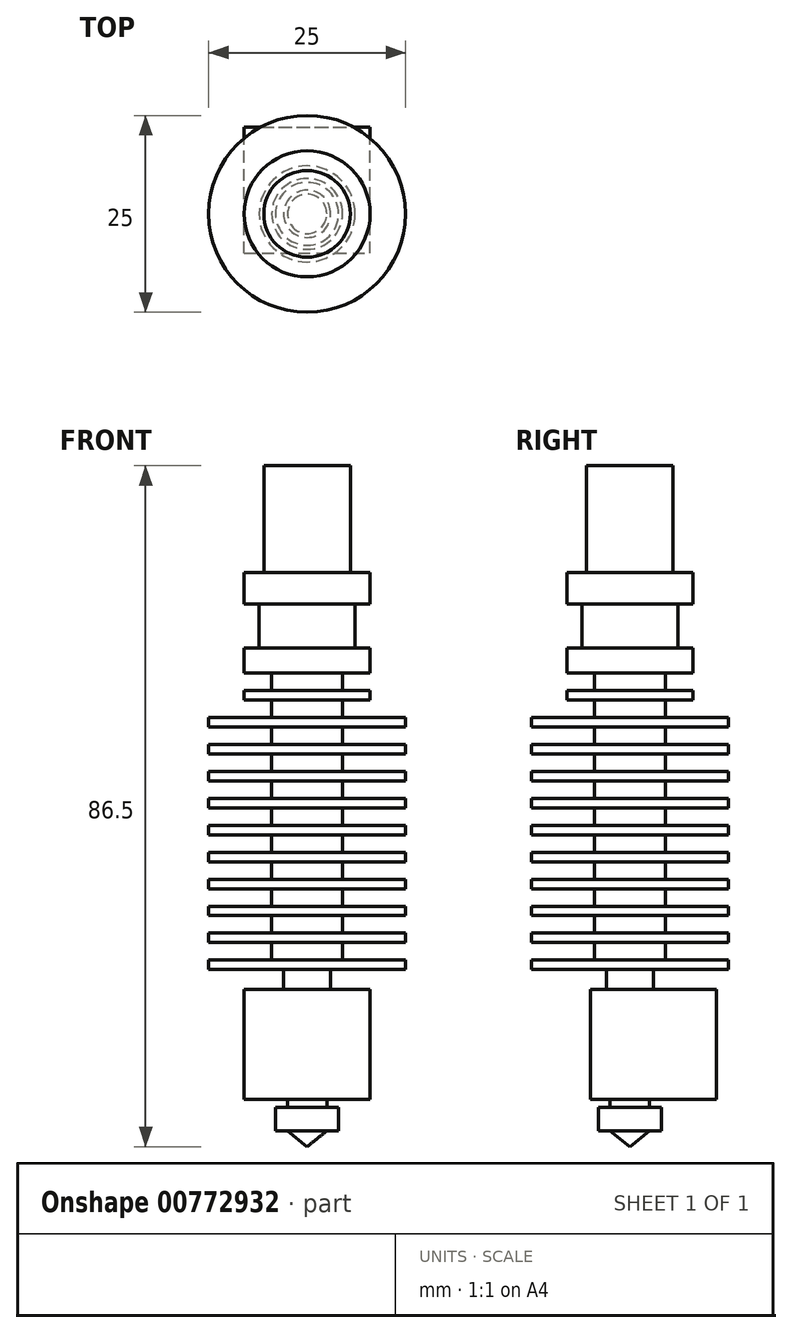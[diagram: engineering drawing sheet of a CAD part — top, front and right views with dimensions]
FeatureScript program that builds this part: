
annotation { "Feature Type Name" : "Feature", "Feature Type Description" : "" }
export const myFeature = defineFeature(function(context is Context, id is Id, definition is map)
    precondition{}
    {
        {
            var Q0;
            Q0=qCreatedBy(makeId("Front.planeOp"),FACE);
            var sketch = newSketch(context, id + "F0", { "sketchPlane" : qUnion([Q0])});
            skLineSegment(sketch, "E0", {"start": v(12.5, 0) * mm, "end": v(12.5, 1.2) * mm});
            skLineSegment(sketch, "E1", {"start": v(12.5, 1.2) * mm, "end": v(4.5, 1.2) * mm});
            skLineSegment(sketch, "E2", {"start": v(4.5, 1.2) * mm, "end": v(4.5, 3.42) * mm});
            skLineSegment(sketch, "E3", {"start": v(4.5, 3.42) * mm, "end": v(12.5, 3.42) * mm});
            skLineSegment(sketch, "E4", {"start": v(12.5, 3.42) * mm, "end": v(12.5, 4.62) * mm});
            skLineSegment(sketch, "E5", {"start": v(12.5, 4.62) * mm, "end": v(4.5, 4.62) * mm});
            skLineSegment(sketch, "E6", {"start": v(4.5, 4.62) * mm, "end": v(4.5, 6.84) * mm});
            skLineSegment(sketch, "E7", {"start": v(4.5, 6.84) * mm, "end": v(12.5, 6.84) * mm});
            skLineSegment(sketch, "E8", {"start": v(12.5, 6.84) * mm, "end": v(12.5, 8.04) * mm});
            skLineSegment(sketch, "E9", {"start": v(12.5, 8.04) * mm, "end": v(4.5, 8.04) * mm});
            skLineSegment(sketch, "E10", {"start": v(4.5, 8.04) * mm, "end": v(4.5, 10.27) * mm});
            skLineSegment(sketch, "E11", {"start": v(4.5, 10.27) * mm, "end": v(12.5, 10.27) * mm});
            skLineSegment(sketch, "E12", {"start": v(12.5, 10.27) * mm, "end": v(12.5, 11.47) * mm});
            skLineSegment(sketch, "E13", {"start": v(12.5, 11.47) * mm, "end": v(4.5, 11.47) * mm});
            skLineSegment(sketch, "E14", {"start": v(4.5, 11.47) * mm, "end": v(4.5, 13.69) * mm});
            skLineSegment(sketch, "E15", {"start": v(4.5, 13.69) * mm, "end": v(12.5, 13.69) * mm});
            skLineSegment(sketch, "E16", {"start": v(12.5, 13.69) * mm, "end": v(12.5, 14.89) * mm});
            skLineSegment(sketch, "E17", {"start": v(12.5, 14.89) * mm, "end": v(4.5, 14.89) * mm});
            skLineSegment(sketch, "E18", {"start": v(4.5, 14.89) * mm, "end": v(4.5, 17.11) * mm});
            skLineSegment(sketch, "E19", {"start": v(4.5, 17.11) * mm, "end": v(12.5, 17.11) * mm});
            skLineSegment(sketch, "E20", {"start": v(12.5, 17.11) * mm, "end": v(12.5, 18.31) * mm});
            skLineSegment(sketch, "E21", {"start": v(12.5, 18.31) * mm, "end": v(4.5, 18.31) * mm});
            skLineSegment(sketch, "E22", {"start": v(4.5, 18.31) * mm, "end": v(4.5, 20.53) * mm});
            skLineSegment(sketch, "E23", {"start": v(4.5, 20.53) * mm, "end": v(12.5, 20.53) * mm});
            skLineSegment(sketch, "E24", {"start": v(12.5, 20.53) * mm, "end": v(12.5, 21.73) * mm});
            skLineSegment(sketch, "E25", {"start": v(12.5, 21.73) * mm, "end": v(4.5, 21.73) * mm});
            skLineSegment(sketch, "E26", {"start": v(4.5, 21.73) * mm, "end": v(4.5, 23.96) * mm});
            skLineSegment(sketch, "E27", {"start": v(4.5, 23.96) * mm, "end": v(12.5, 23.96) * mm});
            skLineSegment(sketch, "E28", {"start": v(12.5, 23.96) * mm, "end": v(12.5, 25.16) * mm});
            skLineSegment(sketch, "E29", {"start": v(12.5, 25.16) * mm, "end": v(4.5, 25.16) * mm});
            skLineSegment(sketch, "E30", {"start": v(4.5, 25.16) * mm, "end": v(4.5, 27.38) * mm});
            skLineSegment(sketch, "E31", {"start": v(4.5, 27.38) * mm, "end": v(12.5, 27.38) * mm});
            skLineSegment(sketch, "E32", {"start": v(12.5, 27.38) * mm, "end": v(12.5, 28.58) * mm});
            skLineSegment(sketch, "E33", {"start": v(12.5, 28.58) * mm, "end": v(4.5, 28.58) * mm});
            skLineSegment(sketch, "E34", {"start": v(4.5, 28.58) * mm, "end": v(4.5, 30.8) * mm});
            skLineSegment(sketch, "E35", {"start": v(4.5, 30.8) * mm, "end": v(12.5, 30.8) * mm});
            skLineSegment(sketch, "E36", {"start": v(12.5, 30.8) * mm, "end": v(12.5, 32) * mm});
            skLineSegment(sketch, "E37", {"start": v(12.5, 32) * mm, "end": v(4.5, 32) * mm});
            skLineSegment(sketch, "E38", {"start": v(4.5, 32) * mm, "end": v(4.5, 34.22) * mm});
            skLineSegment(sketch, "E39", {"start": v(4.5, 34.22) * mm, "end": v(8, 34.22) * mm});
            skLineSegment(sketch, "E40", {"start": v(8, 35.42) * mm, "end": v(4.5, 35.42) * mm});
            skLineSegment(sketch, "E41", {"start": v(4.5, 35.42) * mm, "end": v(4.5, 37.64) * mm});
            skLineSegment(sketch, "E42", {"start": v(4.5, 37.64) * mm, "end": v(8, 37.64) * mm});
            skLineSegment(sketch, "E43", {"start": v(8, 40.84) * mm, "end": v(6.1, 40.84) * mm});
            skLineSegment(sketch, "E44", {"start": v(6.1, 40.84) * mm, "end": v(6.1, 46.44) * mm});
            skLineSegment(sketch, "E45", {"start": v(8, 35.42) * mm, "end": v(8, 34.22) * mm});
            skLineSegment(sketch, "E46", {"start": v(8, 37.64) * mm, "end": v(8, 40.84) * mm});
            skLineSegment(sketch, "E47", {"start": v(8, 50.44) * mm, "end": v(8, 46.44) * mm});
            skLineSegment(sketch, "E48", {"start": v(8, 46.44) * mm, "end": v(6.1, 46.44) * mm});
            skLineSegment(sketch, "E49", {"start": v(0, 64) * mm, "end": v(5.5, 64) * mm});
            skLineSegment(sketch, "E50", {"start": v(5.5, 64) * mm, "end": v(5.5, 50.44) * mm});
            skLineSegment(sketch, "E51", {"start": v(5.5, 50.44) * mm, "end": v(8, 50.44) * mm});
            skLineSegment(sketch, "E52", {"start": v(0, 73.12) * mm, "end": v(0, 7.58) * mm, "construction": true});
            skLineSegment(sketch, "E53", {"start": v(0, -2.5) * mm, "end": v(3, -2.5) * mm});
            skLineSegment(sketch, "E54", {"start": v(3, -2.5) * mm, "end": v(3, 0) * mm});
            skLineSegment(sketch, "E55", {"start": v(3, 0) * mm, "end": v(12.5, 0) * mm});
            skLineSegment(sketch, "E56", {"start": v(0, -2.5) * mm, "end": v(0, 64) * mm});
            skSolve(sketch);
        }
        {
            var Q0;
            Q0=makeQuery(id+"F0.imprint","IMPRINT",FACE,{"disambiguationData":[TD([[makeQuery(id+"F0.imprint","IMPRINT",EDGE,{"derivedFrom":sQuery(id+"F0.wireOp",EDGE,"E0")}),1.0]])]});
            var Q1;
            Q1=sQuery(id+"F0.wireOp",EDGE,"E52");
            revolve(context, id + "F1", {"surfaceOperationType" : NewSurfaceOperationType.NEW, "entities" : qUnion([Q0]), "axis" : qUnion([Q1]), "revolveType" : RevolveType.FULL});
        }
        {
            var Q0;
            Q0=makeQuery(id+"F1.opRevolve","SWEPT_FACE",FACE,{"disambiguationData":[OSD([sQuery(id+"F0.wireOp",EDGE,"E53")])]});
            var sketch = newSketch(context, id + "F2", { "sketchPlane" : qUnion([Q0])});
            skLineSegment(sketch, "E57.bottom", {"start": v(-8, 5) * mm, "end": v(8, 5) * mm});
            skLineSegment(sketch, "E57.top", {"start": v(-8, -11) * mm, "end": v(8, -11) * mm});
            skLineSegment(sketch, "E57.left", {"start": v(-8, 5) * mm, "end": v(-8, -11) * mm});
            skLineSegment(sketch, "E57.right", {"start": v(8, 5) * mm, "end": v(8, -11) * mm});
            skSolve(sketch);
        }
        {
            var Q0;
            Q0 = qSketchRegion(id + "F2", true);
            extrude(context, id + "F3", {"entities" : qUnion([Q0]), "operationType" : NewBodyOperationType.ADD, "depth" : 14 * mm, "offsetDistance" : 25 * mm});
        }
        {
            var Q0;
            Q0=qCreatedBy(makeId("Front.planeOp"),FACE);
            var sketch = newSketch(context, id + "F4", { "sketchPlane" : qUnion([Q0])});
            skLineSegment(sketch, "E58", {"start": v(0, -22.5) * mm, "end": v(2.5, -20.5) * mm});
            skLineSegment(sketch, "E59", {"start": v(2.5, -20.5) * mm, "end": v(4, -20.5) * mm});
            skLineSegment(sketch, "E60", {"start": v(4, -20.5) * mm, "end": v(4, -17.5) * mm});
            skLineSegment(sketch, "E61", {"start": v(4, -17.5) * mm, "end": v(2.5, -17.5) * mm});
            skLineSegment(sketch, "E62", {"start": v(2.5, -17.5) * mm, "end": v(2.5, -16.5) * mm});
            skLineSegment(sketch, "E63", {"start": v(2.5, -16.5) * mm, "end": v(0, -16.5) * mm});
            skLineSegment(sketch, "E64", {"start": v(0, -16.5) * mm, "end": v(0, -22.5) * mm});
            skLineSegment(sketch, "E65", {"start": v(0, -11.25) * mm, "end": v(0, -27.77) * mm, "construction": true});
            skSolve(sketch);
        }
        {
            var Q0;
            Q0=makeQuery(id+"F4.imprint","IMPRINT",FACE,{"disambiguationData":[TD([[makeQuery(id+"F4.imprint","IMPRINT",EDGE,{"derivedFrom":sQuery(id+"F4.wireOp",EDGE,"E58")}),1.0]])]});
            var Q1;
            Q1=sQuery(id+"F4.wireOp",EDGE,"E65");
            revolve(context, id + "F5", {"operationType" : NewBodyOperationType.ADD, "surfaceOperationType" : NewSurfaceOperationType.NEW, "entities" : qUnion([Q0]), "axis" : qUnion([Q1]), "revolveType" : RevolveType.FULL});
        }
    });
